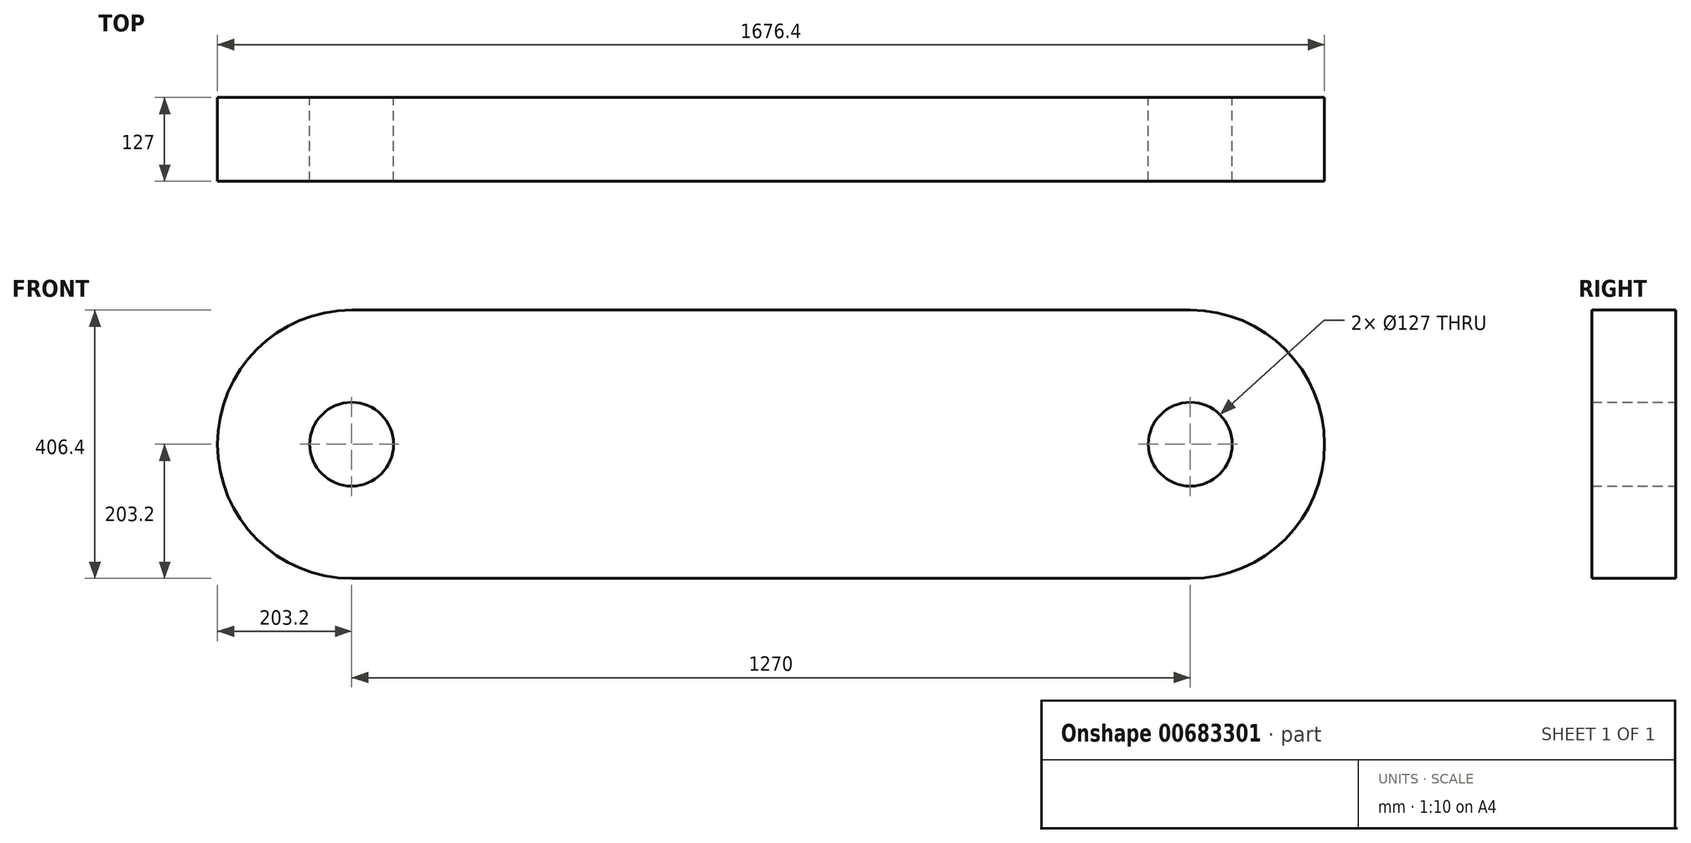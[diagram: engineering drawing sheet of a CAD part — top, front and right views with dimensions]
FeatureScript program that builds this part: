
annotation { "Feature Type Name" : "Feature", "Feature Type Description" : "" }
export const myFeature = defineFeature(function(context is Context, id is Id, definition is map)
    precondition{}
    {
        {
            var Q0;
            Q0=qCreatedBy(makeId("Front.planeOp"),FACE);
            var sketch = newSketch(context, id + "F0", { "sketchPlane" : qUnion([Q0])});
            skLineSegment(sketch, "E0.bottom", {"start": v(-635, 203.2) * mm, "end": v(635, 203.2) * mm});
            skLineSegment(sketch, "E0.top", {"start": v(-635, -203.2) * mm, "end": v(635, -203.2) * mm});
            skArc(sketch, "E1", {"start": v(-635, 203.2) * mm, "mid": v(-838.2, 0) * mm, "end": v(-635, -203.2) * mm});
            skArc(sketch, "E2", {"start": v(635, -203.2) * mm, "mid": v(838.2, 0) * mm, "end": v(635, 203.2) * mm});
            skCircle(sketch, "E3", {"center": v(-635, 0) * mm, "radius": 63.5 * mm});
            skCircle(sketch, "E4", {"center": v(635, 0) * mm, "radius": 63.5 * mm});
            skSolve(sketch);
        }
        {
            var Q0;
            Q0=qSketchRegion(id+"F0",true);
            extrude(context, id + "F1", {"entities" : qUnion([Q0]), "depth" : 127 * mm, "offsetDistance" : 25.4 * mm});
        }
    });
